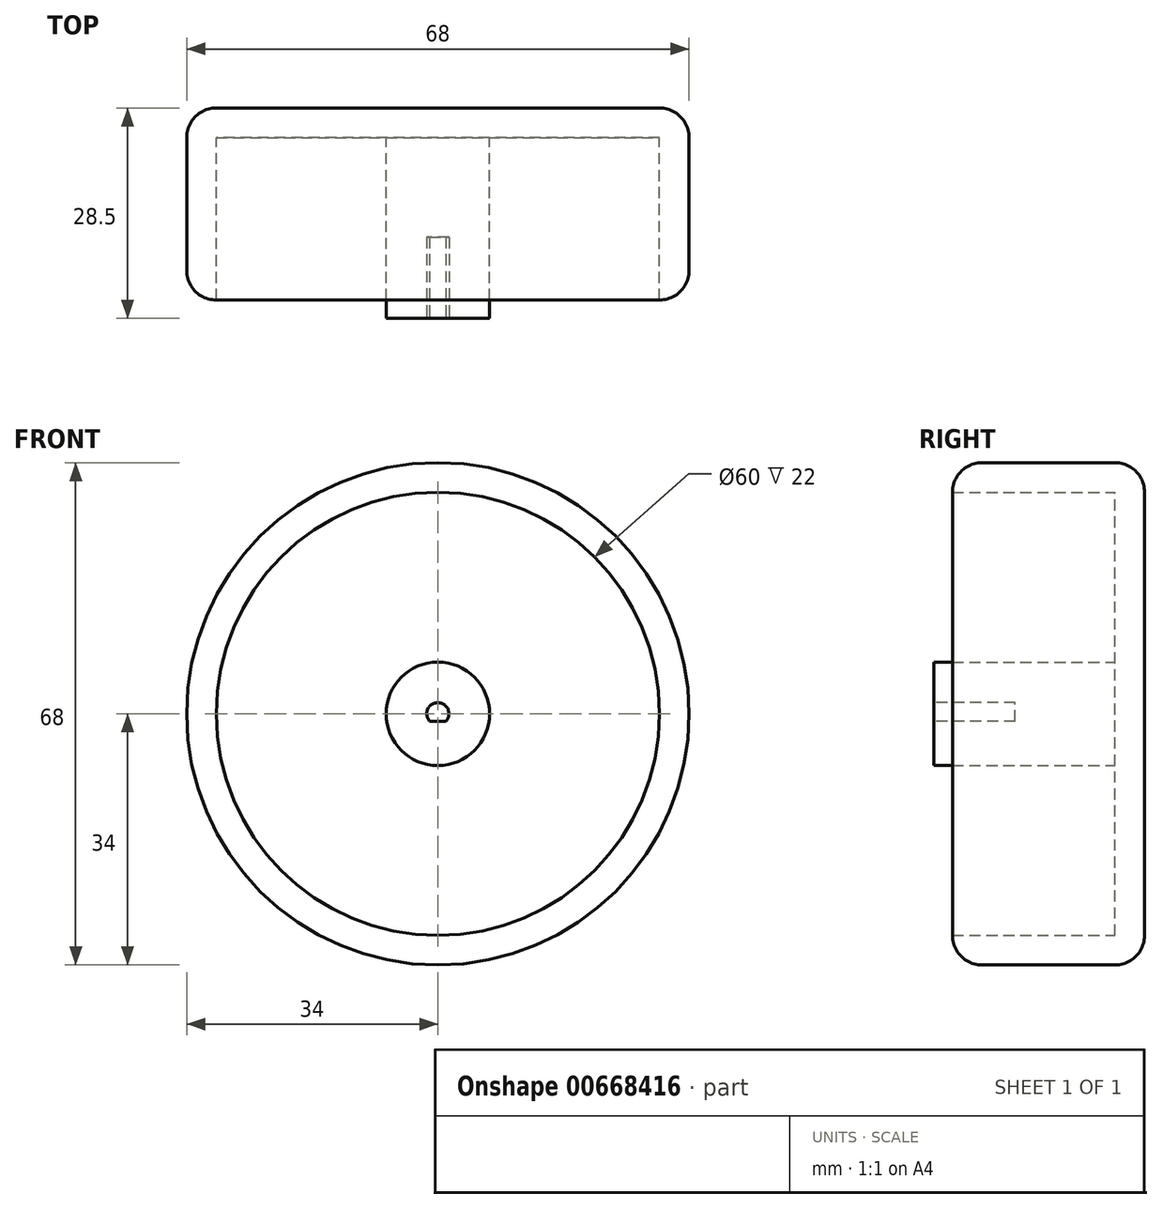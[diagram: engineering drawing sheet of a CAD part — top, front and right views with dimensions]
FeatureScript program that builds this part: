
annotation { "Feature Type Name" : "Feature", "Feature Type Description" : "" }
export const myFeature = defineFeature(function(context is Context, id is Id, definition is map)
    precondition{}
    {
        {
            var Q0;
            Q0=qCreatedBy(makeId("Front.planeOp"),FACE);
            var sketch = newSketch(context, id + "F0", { "sketchPlane" : qUnion([Q0])});
            skCircle(sketch, "E0", {"center": v(0, 0) * mm, "radius": 34 * mm});
            skSolve(sketch);
        }
        {
            var Q0;
            Q0=makeQuery(id+"F0.imprint","IMPRINT",FACE,{"disambiguationData":[TD([[makeQuery(id+"F0.imprint","IMPRINT",EDGE,{"derivedFrom":sQuery(id+"F0.wireOp",EDGE,"E0")}),1.0]])]});
            extrude(context, id + "F1", {"entities" : qUnion([Q0]), "depth" : 26 * mm, "offsetDistance" : 25 * mm});
        }
        {
            var Q0;
            Q0=makeQuery(id+"F1.opExtrude","CAP_EDGE",EDGE,{"disambiguationData":[OSD([sQuery(id+"F0.wireOp",EDGE,"E0")])],"isStart":false});
            var Q1;
            Q1=makeQuery(id+"F1.opExtrude","CAP_EDGE",EDGE,{"disambiguationData":[OSD([sQuery(id+"F0.wireOp",EDGE,"E0")])],"isStart":true});
            fillet(context, id + "F2", {"entities" : qUnion([Q0, Q1]), "radius" : 4 * mm, "tangentPropagation" : true, "allowEdgeOverflow" : false});
        }
        {
            var Q0;
            Q0=makeQuery(id+"F1.opExtrude","CAP_FACE",FACE,{"disambiguationData":[OSD([sQuery(id+"F0.wireOp",EDGE,"E0")])],"isStart":false});
            shell(context, id + "F3", {"entities" : qUnion([Q0]), "thickness" : 4 * mm});
        }
        {
            var Q0;
            {var subQ0=sQuery(id+"F0.wireOp",EDGE,"E0");Q0=makeQuery(id+"F3.opShell","OFFSET_FACE",FACE,{"disambiguationData":[OSD([subQ0]),TDD([makeQuery(id+"F1.opExtrude","CAP_FACE",FACE,{"disambiguationData":[OSD([subQ0])],"isStart":true})])]});}
            var sketch = newSketch(context, id + "F4", { "sketchPlane" : qUnion([Q0])});
            skCircle(sketch, "E1", {"center": v(0, 0) * mm, "radius": 7 * mm});
            skSolve(sketch);
        }
        {
            var Q0;
            Q0=makeQuery(id+"F4.imprint","IMPRINT",FACE,{"disambiguationData":[TD([[makeQuery(id+"F4.imprint","IMPRINT",EDGE,{"derivedFrom":sQuery(id+"F4.wireOp",EDGE,"E1")}),1.0]])]});
            extrude(context, id + "F5", {"entities" : qUnion([Q0]), "operationType" : NewBodyOperationType.ADD, "depth" : 24.5 * mm, "offsetDistance" : 25 * mm});
        }
        {
            var Q0;
            Q0=makeQuery(id+"F5.opExtrude","CAP_FACE",FACE,{"disambiguationData":[OSD([sQuery(id+"F4.wireOp",EDGE,"E1")])],"isStart":false});
            var sketch = newSketch(context, id + "F6", { "sketchPlane" : qUnion([Q0])});
            skCircle(sketch, "E2", {"center": v(0, 0) * mm, "radius": 1.5 * mm});
            skSolve(sketch);
        }
        {
            var Q0;
            Q0=makeQuery(id+"F6.imprint","IMPRINT",FACE,{"disambiguationData":[TD([[makeQuery(id+"F6.imprint","IMPRINT",EDGE,{"derivedFrom":sQuery(id+"F6.wireOp",EDGE,"E2")}),1.0]])]});
            extrude(context, id + "F7", {"entities" : qUnion([Q0]), "operationType" : NewBodyOperationType.ADD, "depth" : 1 * mm, "offsetDistance" : 25 * mm});
        }
        {
            var Q0;
            Q0=makeQuery(id+"F7.opExtrude","CAP_FACE",FACE,{"disambiguationData":[OSD([sQuery(id+"F6.wireOp",EDGE,"E2")])],"isStart":false});
            var sketch = newSketch(context, id + "F8", { "sketchPlane" : qUnion([Q0])});
            skLineSegment(sketch, "E3", {"start": v(0, 1.5) * mm, "end": v(0, -1) * mm});
            skLineSegment(sketch, "E4", {"start": v(-1.12, -1) * mm, "end": v(1.12, -1) * mm});
            skSolve(sketch);
        }
        {
            var Q0;
            {var subQ0=sQuery(id+"F8.wireOp",EDGE,"E4");Q0=makeQuery(id+"F8.imprint","IMPRINT",FACE,{"disambiguationData":[TD([[makeQuery(id+"F8.imprint","IMPRINT",EDGE,{"derivedFrom":subQ0}),1.0]])]});}
            extrude(context, id + "F9", {"entities" : qUnion([Q0]), "operationType" : NewBodyOperationType.REMOVE, "oppositeDirection" : true, "depth" : 12 * mm, "offsetDistance" : 25 * mm});
        }
        {
            var Q0;
            Q0=makeQuery(id+"F7.opExtrude","CAP_FACE",FACE,{"disambiguationData":[OSD([sQuery(id+"F6.wireOp",EDGE,"E2")])],"isStart":false});
            extrude(context, id + "F10", {"entities" : qUnion([Q0]), "operationType" : NewBodyOperationType.REMOVE, "oppositeDirection" : true, "depth" : 1 * mm, "offsetDistance" : 25 * mm});
        }
    });
